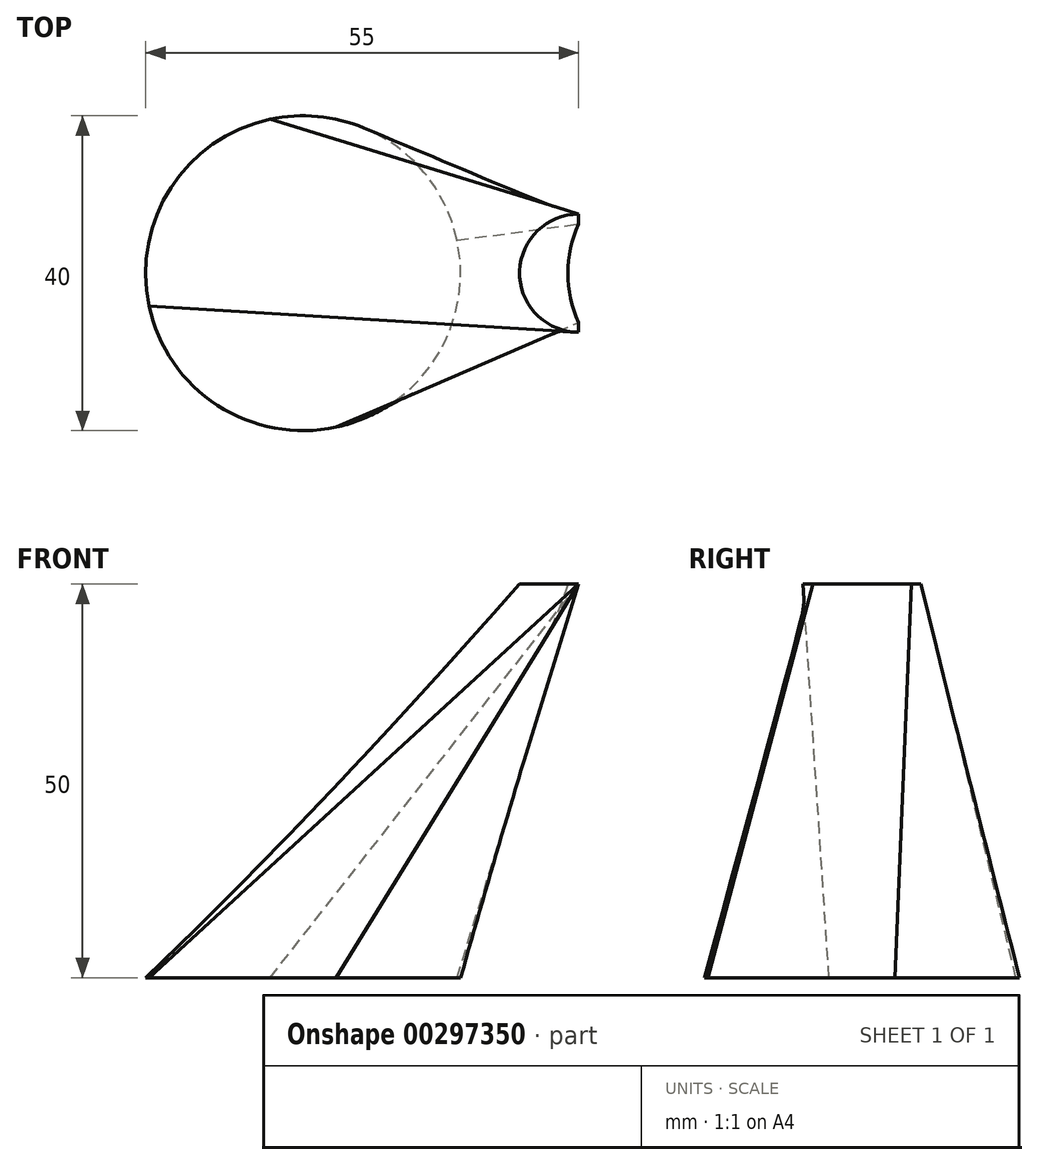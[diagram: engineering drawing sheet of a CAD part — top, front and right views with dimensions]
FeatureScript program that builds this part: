
annotation { "Feature Type Name" : "Feature", "Feature Type Description" : "" }
export const myFeature = defineFeature(function(context is Context, id is Id, definition is map)
    precondition{}
    {
        {
            var Q0;
            Q0=qCreatedBy(makeId("Top.planeOp"),FACE);
            cPlane(context, id + "F0", {"entities" : qUnion([Q0]), "cplaneType" : CPlaneType.OFFSET, "offset" : 50 * mm, "width" : 150 * mm, "height" : 150 * mm});
        }
        {
            var Q0;
            Q0=qCreatedBy(makeId("Top.planeOp"),FACE);
            var sketch = newSketch(context, id + "F1", { "sketchPlane" : qUnion([Q0])});
            skCircle(sketch, "E0", {"center": v(0, 0) * mm, "radius": 20 * mm});
            skSolve(sketch);
        }
        {
            var Q0;
            Q0=qCreatedBy(makeId("Front.planeOp"),FACE);
            var sketch = newSketch(context, id + "F2", { "sketchPlane" : qUnion([Q0])});
            skLineSegment(sketch, "E1", {"start": v(0, 0) * mm, "end": v(35, 50) * mm, "construction": true});
            skSolve(sketch);
        }
        {
            var Q0;
            Q0=qCreatedBy(id+"F0.planeOp",FACE);
            var sketch = newSketch(context, id + "F3", { "sketchPlane" : qUnion([Q0])});
            skArc(sketch, "E2", {"start": v(35, 7.5) * mm, "mid": v(27.5, 0) * mm, "end": v(35, -7.5) * mm});
            skLineSegment(sketch, "E3", {"start": v(35, -7.5) * mm, "end": v(35, -6.25) * mm});
            skLineSegment(sketch, "E4.trimOffspring", {"start": v(35, 6.25) * mm, "end": v(35, 7.5) * mm});
            skArc(sketch, "E5", {"start": v(35, 6.25) * mm, "mid": v(33.64, 0) * mm, "end": v(35, -6.25) * mm});
            skSolve(sketch);
        }
        {
            var Q0;
            Q0 = qSketchRegion(id + "F1", true);
            var Q1;
            Q1 = qSketchRegion(id + "F3", true);
            loft(context, id + "F4", {"sheetProfilesArray" : [{ "sheetProfileEntities" : qUnion([Q0]) }, { "sheetProfileEntities" : qUnion([Q1]) }]});
        }
    });
